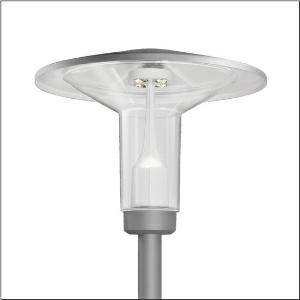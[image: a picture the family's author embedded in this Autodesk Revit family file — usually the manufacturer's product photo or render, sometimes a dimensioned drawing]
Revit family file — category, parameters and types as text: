
# Revit family: laterne_iq___st1_2a_5xa5255kf14h_a0c9
name_source: partatom
category: Lighting Fixtures
units: mm (PartAtom-declared; Revit-internal decimal feet)

## family parameters
Cut with Voids When Loaded = No
Host = Face
Light Source = No
Part Type = Normal
Room Calculation Point = No
Round Connector Dimension = Use Diameter
Shared = No

## types (1)
- --- (1 x LED, 1540 lm, 10 W, 4000K)
    Apparent Load = 10 VA
    CIE Flux Codes = 25 63 94 98 100
    Color Rendering = 70
    Color Temperature = 4000K
    Default Elevation = 1800 mm
    Description = Lantern iQ, mast luminaire, Module 540 iQ-SR, primary light control with 3 zone facetted reflector, of plastic, silver coated, highly specular, structured, primary optical cover: cover, of PMMA, transparent, light distribution: ST1.2a, light emission: direct distribution, primary light characteristic: asymmetric, installation type: post-top, LED, High Power LED, rated luminous flux: 1.540lm, luminous efficacy: 154lm/W, light colour: 740, colour temperature: 4000K, control gear: ECG iQ, control: presetting dimming logarithmic, Street-Remote, Auto-Match, Temp-Guard, Lumen-Switch, Night-Set, Smart-Wire, Light-Fading, Desk-Remote (wireless, voltage-free reading and setting of iQ features in the workshop via application-optimized NFC function/RFID function), optimised constant luminous flux control (CLO 2.0), with terminal, 6-pole, max. 2.5mm², mains connection: 230..240V, AC, 50/60Hz, start of lifetime: 10W, end of service life: 10W, reduction: 5W, luminaire housing, upper part, of glass-fibre reinforced polyester, coated, Siteco® metallic grey (DB 702S), diameter: 750mm, height: 583mm, spigot size: d x l = 76 x 70mm (post-top) | with reducer (optional accessory) 60 x 70mm, post-top mast mounting element, of diecast aluminium, coated, Siteco® metallic grey (DB 702S), Module 540 iQ-SR, traffic white (RAL 9016), equipment: standard, protection rating (complete): IP65, insulation class (complete): insulation class II (safety insulation), certification: CE, ENEC, VDE, packaging unit: 1 piece

Light Distribution: ST1.2a
    Height = 583 mm
    Lamp = 1 x LED
    Lamp Light Flux = 1540 lm
    Lamp Power = 10 W
    Lamp count = 1
    Length = 750 mm
    Luminous efficacy = 154 lm/W
    Manufacturer = Siteco
    ModVariant = No
    Model = 5XA5255KF14H
    Number of Poles = 1
    OnlyDefault = Yes
    Power Factor = 1
    Product Name = Laterne iQ | ST1.2a
    Product group = mast luminaire | pylon top
    ProductGroupID = 6100
    Protection Class = Protection class II
    Protection Degree = IP 65
    RLX_Detail_Level = 1
    RLX_Emergency_Light_Flux = 0 lm
    RLX_Emergency_Type = 0
    RLX_Emergency_Type_DB = No
    RlxData = <blob elided: 107029 chars, md5=34802bd8>
    Socket = socket
    Standby Power = 0 W
    System Light Flux = 1540 lm
    System Power = 10 W
    Type Comments = factory setting: luminous flux: 100 % | dim-lin: 254 | 401 mA
    Type Image = l_1006050.jpg
    URL = http://relux.com
    VarID = @adj_110779
    Voltage = 0 V
    Weight = 0.00 kg
    Width = 0 mm  [stored 0 ft]

note: [stored X ft] marks values corroborated as IEEE doubles in the binary element streams (Revit-internal decimal feet)

## geometry (parser evidence)
native form markers: Blend x4, Sweep x11
no freeform markers — native parametric forms only
